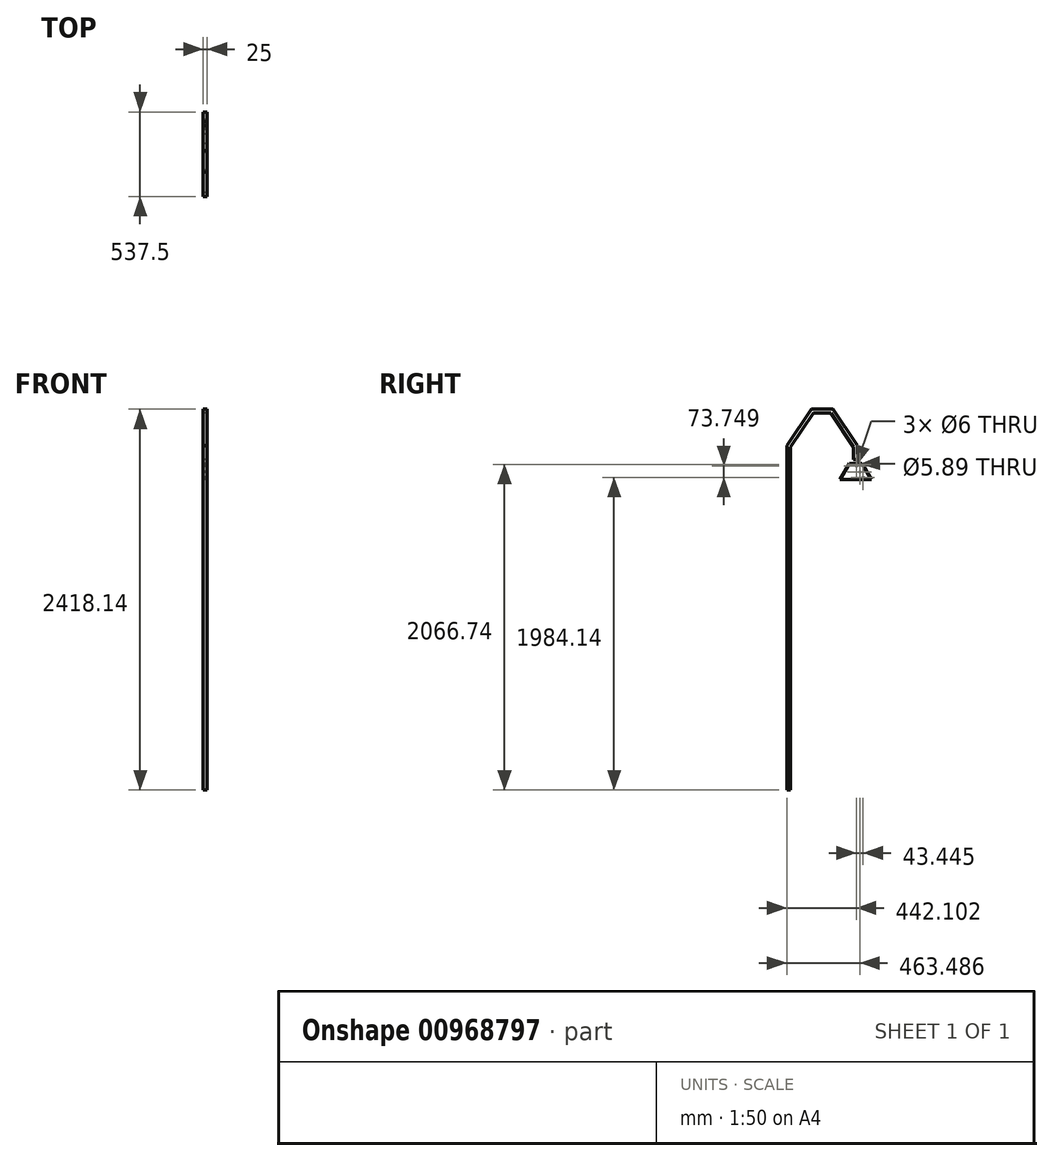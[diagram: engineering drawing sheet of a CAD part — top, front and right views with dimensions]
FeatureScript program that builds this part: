
annotation { "Feature Type Name" : "Feature", "Feature Type Description" : "" }
export const myFeature = defineFeature(function(context is Context, id is Id, definition is map)
    precondition{}
    {
        {
            var Q0;
            Q0=qCreatedBy(makeId("Right.planeOp"),FACE);
            var sketch = newSketch(context, id + "F0", { "sketchPlane" : qUnion([Q0])});
            skLineSegment(sketch, "E0", {"start": v(3.68, 1908.52) * mm, "end": v(160.39, 2140.85) * mm});
            skLineSegment(sketch, "E1", {"start": v(160.39, 2140.85) * mm, "end": v(296.97, 2140.85) * mm});
            skLineSegment(sketch, "E2", {"start": v(296.97, 2140.85) * mm, "end": v(453.68, 1908.52) * mm});
            skLineSegment(sketch, "E3.0", {"start": v(283.68, 2115.85) * mm, "end": v(428.68, 1900.88) * mm});
            skLineSegment(sketch, "E3.1", {"start": v(173.68, 2115.85) * mm, "end": v(283.68, 2115.85) * mm});
            skLineSegment(sketch, "E3.2", {"start": v(28.68, 1900.88) * mm, "end": v(173.68, 2115.85) * mm});
            skLineSegment(sketch, "E4", {"start": v(28.68, 1900.88) * mm, "end": v(3.68, 1908.52) * mm});
            skLineSegment(sketch, "E5", {"start": v(173.68, 2115.85) * mm, "end": v(160.39, 2140.85) * mm});
            skLineSegment(sketch, "E6", {"start": v(283.68, 2115.85) * mm, "end": v(296.97, 2140.85) * mm});
            skLineSegment(sketch, "E7", {"start": v(428.68, 1900.88) * mm, "end": v(453.68, 1908.52) * mm});
            skLineSegment(sketch, "E8", {"start": v(453.68, 1821.63) * mm, "end": v(428.68, 1821.63) * mm});
            skLineSegment(sketch, "E9", {"start": v(428.68, 1821.63) * mm, "end": v(428.68, 1900.88) * mm});
            skLineSegment(sketch, "E10", {"start": v(453.68, 1908.52) * mm, "end": v(453.68, 1821.63) * mm});
            skLineSegment(sketch, "E11", {"start": v(3.68, 1908.52) * mm, "end": v(3.68, -277.3) * mm});
            skLineSegment(sketch, "E12", {"start": v(28.68, 1900.88) * mm, "end": v(28.68, -277.3) * mm});
            skLineSegment(sketch, "E13", {"start": v(341.18, 1692.7) * mm, "end": v(401.18, 1796.63) * mm});
            skLineSegment(sketch, "E14", {"start": v(401.18, 1796.63) * mm, "end": v(481.18, 1796.63) * mm});
            skLineSegment(sketch, "E15", {"start": v(481.18, 1796.63) * mm, "end": v(541.18, 1692.7) * mm});
            skLineSegment(sketch, "E16", {"start": v(541.18, 1692.7) * mm, "end": v(341.18, 1692.7) * mm});
            skLineSegment(sketch, "E17", {"start": v(3.68, -277.3) * mm, "end": v(28.68, -277.3) * mm});
            skLineSegment(sketch, "E18", {"start": v(401.18, 1796.63) * mm, "end": v(412.47, 1781.07) * mm});
            skLineSegment(sketch, "E19", {"start": v(412.47, 1781.07) * mm, "end": v(474.97, 1781.07) * mm});
            skLineSegment(sketch, "E20", {"start": v(474.97, 1781.07) * mm, "end": v(481.18, 1796.63) * mm});
            skLineSegment(sketch, "E21", {"start": v(401.18, 1796.63) * mm, "end": v(410.84, 1779.9) * mm});
            skLineSegment(sketch, "E22", {"start": v(410.84, 1779.9) * mm, "end": v(364.23, 1699.16) * mm});
            skLineSegment(sketch, "E23", {"start": v(364.23, 1699.16) * mm, "end": v(341.18, 1692.7) * mm});
            skLineSegment(sketch, "E24", {"start": v(481.18, 1796.63) * mm, "end": v(476.08, 1779.9) * mm});
            skLineSegment(sketch, "E25", {"start": v(476.08, 1779.9) * mm, "end": v(522.7, 1699.16) * mm});
            skLineSegment(sketch, "E26", {"start": v(522.7, 1699.16) * mm, "end": v(541.18, 1692.7) * mm});
            skCircle(sketch, "E27", {"center": v(381.15, 1788.64) * mm, "radius": 3 * mm});
            skCircle(sketch, "E28", {"center": v(467.17, 1789.44) * mm, "radius": 2.94 * mm});
            skCircle(sketch, "E29", {"center": v(363.72, 1781.13) * mm, "radius": 3 * mm});
            skCircle(sketch, "E30", {"center": v(319.74, 1704.97) * mm, "radius": 3 * mm});
            skCircle(sketch, "E31", {"center": v(341.2, 1741.44) * mm, "radius": 2.95 * mm});
            skCircle(sketch, "E32", {"center": v(445.78, 1780.6) * mm, "radius": 3 * mm});
            skCircle(sketch, "E33", {"center": v(468.3, 1741.44) * mm, "radius": 3 * mm});
            skCircle(sketch, "E34", {"center": v(489.23, 1706.85) * mm, "radius": 3 * mm});
            skLineSegment(sketch, "E35.bottom", {"start": v(428.68, 1796.63) * mm, "end": v(453.68, 1796.63) * mm});
            skLineSegment(sketch, "E35.top", {"start": v(428.68, 1821.63) * mm, "end": v(453.68, 1821.63) * mm});
            skLineSegment(sketch, "E35.left", {"start": v(428.68, 1796.63) * mm, "end": v(428.68, 1821.63) * mm});
            skLineSegment(sketch, "E35.right", {"start": v(453.68, 1796.63) * mm, "end": v(453.68, 1821.63) * mm});
            skLineSegment(sketch, "E36.bottom", {"start": v(612.06, 1692.7) * mm, "end": v(1612.06, 1692.7) * mm});
            skLineSegment(sketch, "E36.top", {"start": v(671.93, 1796.7) * mm, "end": v(1552.2, 1796.7) * mm});
            skLineSegment(sketch, "E36.left", {"start": v(612.06, 1796.63) * mm, "end": v(612.06, 1796.7) * mm});
            skLineSegment(sketch, "E37", {"start": v(612.06, 1692.7) * mm, "end": v(671.93, 1796.7) * mm});
            skLineSegment(sketch, "E38", {"start": v(1612.06, 1692.7) * mm, "end": v(1552.2, 1796.7) * mm});
            skPoint(sketch, "E39.end.orphan", {"position": v(612.06, 1796.63) * mm});
            skLineSegment(sketch, "E40.bottom", {"start": v(811.93, 1796.7) * mm, "end": v(1411.93, 1796.7) * mm});
            skLineSegment(sketch, "E40.top", {"start": v(811.93, 1821.7) * mm, "end": v(1411.93, 1821.7) * mm});
            skLineSegment(sketch, "E40.left", {"start": v(811.93, 1796.7) * mm, "end": v(811.93, 1821.7) * mm});
            skLineSegment(sketch, "E40.right", {"start": v(1411.93, 1796.7) * mm, "end": v(1411.93, 1821.7) * mm});
            skLineSegment(sketch, "E41.bottom", {"start": v(936.93, 1821.7) * mm, "end": v(961.93, 1821.7) * mm});
            skLineSegment(sketch, "E41.top", {"start": v(936.93, 1908.7) * mm, "end": v(961.93, 1908.7) * mm});
            skLineSegment(sketch, "E41.left", {"start": v(936.93, 1821.7) * mm, "end": v(936.93, 1908.7) * mm});
            skLineSegment(sketch, "E41.right", {"start": v(961.93, 1821.7) * mm, "end": v(961.93, 1908.7) * mm});
            skLineSegment(sketch, "E42.bottom", {"start": v(1261.93, 1821.7) * mm, "end": v(1286.93, 1821.7) * mm});
            skLineSegment(sketch, "E42.top", {"start": v(1261.93, 1908.7) * mm, "end": v(1286.93, 1908.7) * mm});
            skLineSegment(sketch, "E42.left", {"start": v(1261.93, 1821.7) * mm, "end": v(1261.93, 1908.7) * mm});
            skLineSegment(sketch, "E42.right", {"start": v(1286.93, 1821.7) * mm, "end": v(1286.93, 1908.7) * mm});
            skSolve(sketch);
        }
        {
            var Q0;
            Q0=makeQuery(id+"F0.imprint","IMPRINT",FACE,{"disambiguationData":[TD([[makeQuery(id+"F0.imprint","IMPRINT",EDGE,{"derivedFrom":sQuery(id+"F0.wireOp",EDGE,"E4")}),1.0]])]});
            var Q1;
            Q1=makeQuery(id+"F0.imprint","IMPRINT",FACE,{"disambiguationData":[TD([[makeQuery(id+"F0.imprint","IMPRINT",EDGE,{"derivedFrom":sQuery(id+"F0.wireOp",EDGE,"E0")}),-1.0]])]});
            var Q2;
            Q2=makeQuery(id+"F0.imprint","IMPRINT",FACE,{"disambiguationData":[TD([[makeQuery(id+"F0.imprint","IMPRINT",EDGE,{"derivedFrom":sQuery(id+"F0.wireOp",EDGE,"E1")}),-1.0]])]});
            var Q3;
            Q3=makeQuery(id+"F0.imprint","IMPRINT",FACE,{"disambiguationData":[TD([[makeQuery(id+"F0.imprint","IMPRINT",EDGE,{"derivedFrom":sQuery(id+"F0.wireOp",EDGE,"E2")}),-1.0]])]});
            var Q4;
            Q4=makeQuery(id+"F0.imprint","IMPRINT",FACE,{"disambiguationData":[TD([[makeQuery(id+"F0.imprint","IMPRINT",EDGE,{"derivedFrom":sQuery(id+"F0.wireOp",EDGE,"E7")}),-1.0]])]});
            var Q5;
            Q5=makeQuery(id+"F0.imprint","IMPRINT",FACE,{"disambiguationData":[TD([[makeQuery(id+"F0.imprint","IMPRINT",EDGE,{"derivedFrom":sQuery(id+"F0.wireOp",EDGE,"E35.bottom")}),1.0]])]});
            var Q6;
            Q6=makeQuery(id+"F0.imprint","IMPRINT",FACE,{"disambiguationData":[TD([[makeQuery(id+"F0.imprint","IMPRINT",EDGE,{"derivedFrom":sQuery(id+"F0.wireOp",EDGE,"E16")}),-1.0]])]});
            var Q7;
            Q7=makeQuery(id+"F0.imprint","IMPRINT",FACE,{"disambiguationData":[TD([[makeQuery(id+"F0.imprint","IMPRINT",EDGE,{"derivedFrom":sQuery(id+"F0.wireOp",EDGE,"E15")}),-1.0]])]});
            var Q8;
            {var subQ1=sQuery(id+"F0.wireOp",EDGE,"E18");Q8=makeQuery(id+"F0.imprint","IMPRINT",FACE,{"disambiguationData":[TD([[makeQuery(id+"F0.imprint","IMPRINT",EDGE,{"derivedFrom":subQ1}),1.0]])]});}
            var Q9;
            Q9=makeQuery(id+"F0.imprint","IMPRINT",FACE,{"disambiguationData":[TD([[makeQuery(id+"F0.imprint","IMPRINT",EDGE,{"derivedFrom":sQuery(id+"F0.wireOp",EDGE,"E13")}),-1.0]])]});
            extrude(context, id + "F1", {"entities" : qUnion([Q0, Q1, Q2, Q3, Q4, Q5, Q6, Q7, Q8, Q9]), "depth" : 25 * mm, "offsetDistance" : 25 * mm});
        }
    });
